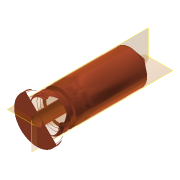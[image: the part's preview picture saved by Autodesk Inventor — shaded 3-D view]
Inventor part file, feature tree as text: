
AUTODESK INVENTOR PART (.ipt)
format: ipt  version: 2016 (Build 200138000, 138)  size: 174,592 bytes
history: native  units: mm
features: sketch x6, extrude x3, revolve x3, reference x2, chamfer x1
ambient origin geometry x8: Origin, YZ Plane, XZ Plane, XY Plane, X Axis, Y Axis, Z Axis, Center Point
bodies: Solid1 (feature_tree)
feature tree (15):
  extrude  "Extrusion1"  Depth=1.0mm TaperAngle=0.0deg
  extrude  "Extrusion2"  Depth=15.5mm TaperAngle=0.0deg
  extrude  "Extrusion3"  Depth=2.0mm TaperAngle=0.0deg
  revolve  "Revolution1"  [1 undecoded]
  revolve  "Revolution2"  Angle=90.0deg
  chamfer  "Chamfer1"  Angle=90.0deg  [1 undecoded]
  revolve  "Revolution3"  Angle=45.0deg
  sketch  "Sketch1"  dims[d0=8.0mm d1=1.0mm d2=0.0mm]
  sketch  "Sketch2"  dims[d3=6.0mm d4=15.5mm d5=0.0mm]
  sketch  "Sketch3"  dims[d6=2.0mm d7=21.0mm d8=0.0mm]
  sketch  "Sketch4"  dims[d9=6.981317mm d10=0.2mm]
  sketch  "Sketch5"  dims[d11=30.0deg d13=90.0deg]
  sketch  "Sketch6"  dims[d14=0.7mm d15=90.0deg d16=0.3mm d17=2.0mm d18=45.0deg d19=45.0deg d20=0.05mm d21=1.0mm d22=0.6mm d23=90.0deg]
  reference  "Reference1"
  reference  "Reference2"
note: 2 required parameter values undecoded (feature->parameter linkage not recoverable at this tier; creation-order binding heuristic only, values carry confidence <= 0.55)